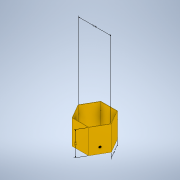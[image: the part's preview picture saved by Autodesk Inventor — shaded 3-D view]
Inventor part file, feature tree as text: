
AUTODESK INVENTOR PART (.ipt)
format: ipt  version: 2022 (Build 260153000, 153)  size: 207,360 bytes
history: native  units: in
note: dims shown in document units (in); Inventor stores cm internally (conversion verified against a paired STEP export)
features: extrude x5, sketch x5, other x4, thread x3, shell x1
ambient origin geometry x8: Origin, YZ Plane, XZ Plane, XY Plane, X Axis, Y Axis, Z Axis, Center Point
bodies: Solid1 (feature_tree)
feature tree (18):
  other  "Annotations"
  extrude  "Extrusion1"  Depth=0.125in
  shell  "Shell1"  Thickness=0.125in
  extrude  "Extrusion2"  Depth=0.125in
  extrude  "Extrusion3"  Depth=2.0in
  thread  "Thread1"  [1 undecoded]
  thread  "Thread2"  [1 undecoded]
  thread  "Thread3"  [1 undecoded]
  sketch  "Sketch4"  dims[d26=0.138in d27=0.138in]
  sketch  "Sketch5"  dims[d28=0.794in d29=0.794in d30=0.5in d31=0.0in d32=0.125in d33=0.0in d34=0.125in d35=0.0in d36=0.125in d37=0.0in d38=5.35in d39=3.0in d40=0.1417in d41=5.35in d42=3.0in d43=0.1417in d44=1.0in d45=0.0in d46=1.0in d47=0.0in d10=0.1768in d11=8.25in d12=0.2072in d13=0.3103in d14=10.931in d6=0.2098in d7=0.199in d8=5.6098in d9=0.1556in]
  extrude  "Extrusion4"  Depth=0.138in
  extrude  "Extrusion5"  Depth=5.6098in
  sketch  "Sketch1"  dims[d0=7.5in d1=1.0in d2=0.125in]
  sketch  "Sketch2"  dims[d3=8.25in d4=0.0in d5=0.125in]
  sketch  "Sketch3"  dims[d15=0.75in d16=2.0in d17=1.0in d18=0.0in d20=0.138in d21=0.794in]
  other  "Linear Dimension 1"
  other  "Linear Dimension 2"
  other  "Linear Dimension 3"
note: 3 required parameter values undecoded (feature->parameter linkage not recoverable at this tier; creation-order binding heuristic only, values carry confidence <= 0.55)
